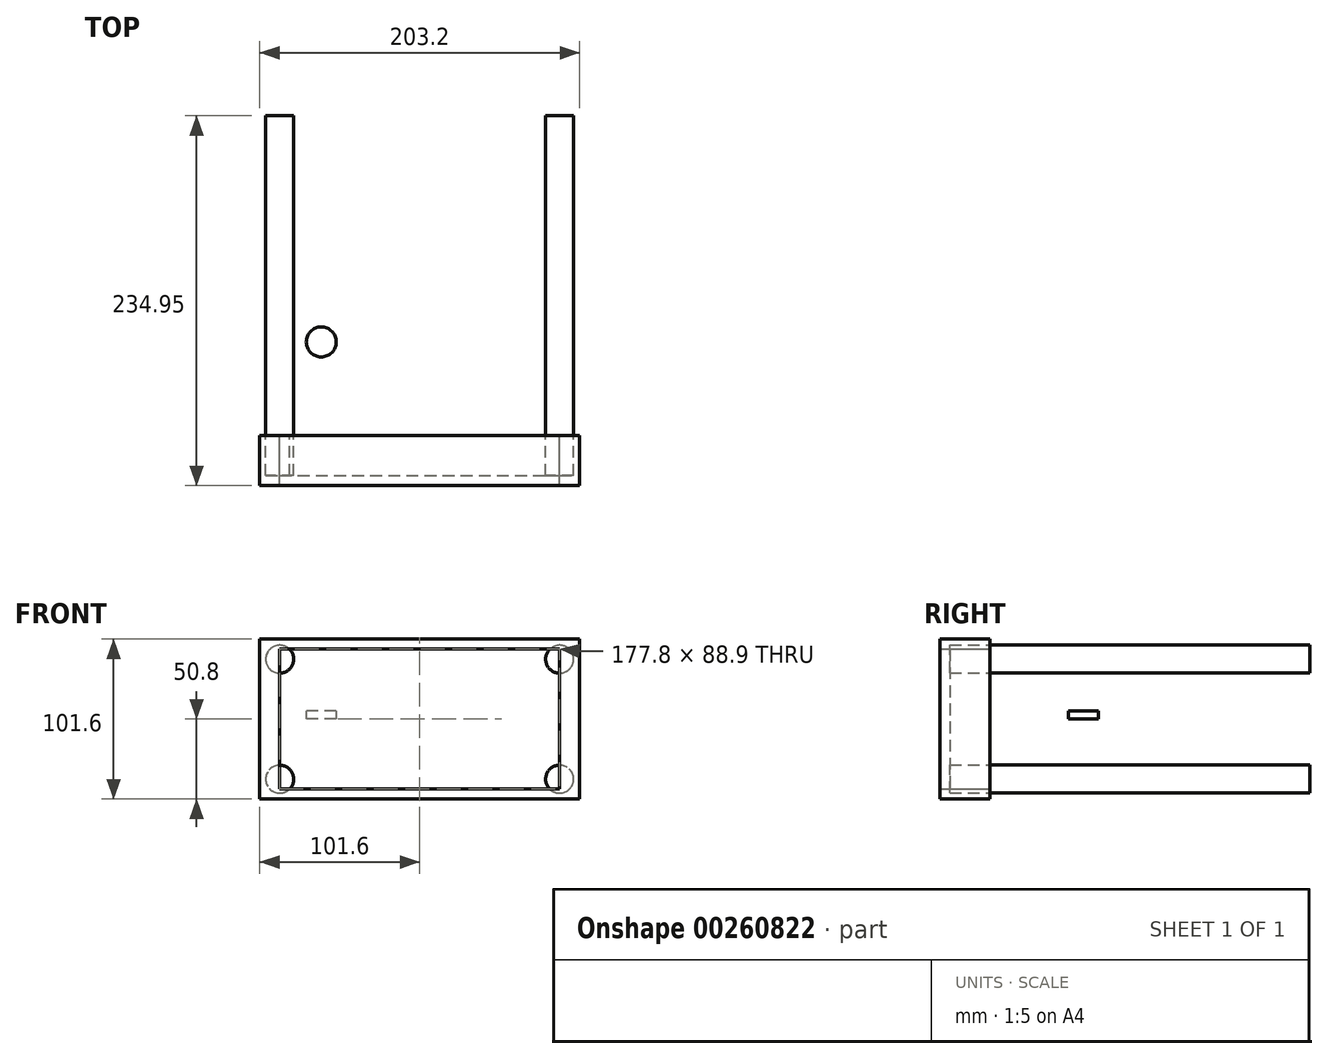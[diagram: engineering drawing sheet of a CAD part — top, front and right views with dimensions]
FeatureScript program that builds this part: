
annotation { "Feature Type Name" : "Feature", "Feature Type Description" : "" }
export const myFeature = defineFeature(function(context is Context, id is Id, definition is map)
    precondition{}
    {
        {
            var Q0;
            Q0=qCreatedBy(makeId("Front.planeOp"),FACE);
            var sketch = newSketch(context, id + "F0", { "sketchPlane" : qUnion([Q0])});
            skLineSegment(sketch, "E0.bottom", {"start": v(-101.6, 50.8) * mm, "end": v(101.6, 50.8) * mm});
            skLineSegment(sketch, "E0.top", {"start": v(-101.6, -50.8) * mm, "end": v(101.6, -50.8) * mm});
            skLineSegment(sketch, "E0.left", {"start": v(-101.6, 50.8) * mm, "end": v(-101.6, -50.8) * mm});
            skLineSegment(sketch, "E0.right", {"start": v(101.6, 50.8) * mm, "end": v(101.6, -50.8) * mm});
            skPoint(sketch, "E0.middle", {"position": v(0, 0) * mm});
            skLineSegment(sketch, "E1.bottom", {"start": v(-88.9, 44.45) * mm, "end": v(88.9, 44.45) * mm});
            skLineSegment(sketch, "E1.top", {"start": v(-88.9, -44.45) * mm, "end": v(88.9, -44.45) * mm});
            skLineSegment(sketch, "E1.left", {"start": v(-88.9, 44.45) * mm, "end": v(-88.9, -44.45) * mm});
            skLineSegment(sketch, "E1.right", {"start": v(88.9, 44.45) * mm, "end": v(88.9, -44.45) * mm});
            skCircle(sketch, "E2", {"center": v(-88.9, 38.1) * mm, "radius": 8.9 * mm});
            skCircle(sketch, "E3", {"center": v(-88.9, -38.1) * mm, "radius": 8.9 * mm});
            skCircle(sketch, "E4", {"center": v(88.9, 38.1) * mm, "radius": 8.9 * mm});
            skCircle(sketch, "E5", {"center": v(88.9, -38.1) * mm, "radius": 8.9 * mm});
            skSolve(sketch);
        }
        {
            var Q0;
            Q0 = qSketchRegion(id + "F0", true);
            var Q1;
            {var subQ0=sQuery(id+"F0.wireOp",EDGE,"E1.left");var subQ1=sQuery(id+"F0.wireOp",EDGE,"E1.bottom");var subQ2=makeQuery(id+"F0.imprint","INTERSECT",VERTEX,{"derivedFrom":[subQ1,subQ0]});Q1=makeQuery(id+"F0.imprint","IMPRINT",FACE,{"disambiguationData":[TD([[makeQuery(id+"F0.imprint","IMPRINT",EDGE,{"disambiguationData":[TD([[subQ2,-1.0]])],"derivedFrom":subQ1}),1.0]])]});}
            var Q2;
            {var subQ0=sQuery(id+"F0.wireOp",EDGE,"E1.left");var subQ1=sQuery(id+"F0.wireOp",EDGE,"E1.top");var subQ2=makeQuery(id+"F0.imprint","INTERSECT",VERTEX,{"derivedFrom":[subQ1,subQ0]});Q2=makeQuery(id+"F0.imprint","IMPRINT",FACE,{"disambiguationData":[TD([[makeQuery(id+"F0.imprint","IMPRINT",EDGE,{"disambiguationData":[TD([[subQ2,-1.0]])],"derivedFrom":subQ1}),-1.0]])]});}
            var Q3;
            {var subQ0=sQuery(id+"F0.wireOp",EDGE,"E1.right");var subQ1=sQuery(id+"F0.wireOp",EDGE,"E1.top");var subQ2=makeQuery(id+"F0.imprint","INTERSECT",VERTEX,{"derivedFrom":[subQ1,subQ0]});Q3=makeQuery(id+"F0.imprint","IMPRINT",FACE,{"disambiguationData":[TD([[makeQuery(id+"F0.imprint","IMPRINT",EDGE,{"disambiguationData":[TD([[subQ2,1.0]])],"derivedFrom":subQ1}),-1.0]])]});}
            var Q4;
            {var subQ0=sQuery(id+"F0.wireOp",EDGE,"E1.right");var subQ1=sQuery(id+"F0.wireOp",EDGE,"E1.bottom");var subQ2=makeQuery(id+"F0.imprint","INTERSECT",VERTEX,{"derivedFrom":[subQ1,subQ0]});Q4=makeQuery(id+"F0.imprint","IMPRINT",FACE,{"disambiguationData":[TD([[makeQuery(id+"F0.imprint","IMPRINT",EDGE,{"disambiguationData":[TD([[subQ2,1.0]])],"derivedFrom":subQ1}),1.0]])]});}
            extrude(context, id + "F1", {"entities" : qUnion([Q0, Q1, Q2, Q3, Q4]), "depth" : 31.75 * mm});
        }
        {
            var Q0;
            Q0=makeQuery(id+"F0.imprint","IMPRINT",FACE,{"disambiguationData":[TD([[makeQuery(id+"F0.imprint","IMPRINT",EDGE,{"derivedFrom":sQuery(id+"F0.wireOp",EDGE,"E1.bottom")}),-1.0]])]});
            var Q1;
            {var subQ0=sQuery(id+"F0.wireOp",EDGE,"E1.right");var subQ1=sQuery(id+"F0.wireOp",EDGE,"E1.bottom");var subQ2=makeQuery(id+"F0.imprint","INTERSECT",VERTEX,{"derivedFrom":[subQ1,subQ0]});Q1=makeQuery(id+"F0.imprint","IMPRINT",FACE,{"disambiguationData":[TD([[makeQuery(id+"F0.imprint","IMPRINT",EDGE,{"disambiguationData":[TD([[subQ2,1.0]])],"derivedFrom":subQ1}),1.0]])]});}
            extrude(context, id + "F2", {"entities" : qUnion([Q0, Q1]), "depth" : 25.4 * mm});
        }
        {
            var Q0;
            {var subQ0=sQuery(id+"F0.wireOp",EDGE,"E1.left");var subQ1=sQuery(id+"F0.wireOp",EDGE,"E1.bottom");var subQ2=makeQuery(id+"F0.imprint","INTERSECT",VERTEX,{"derivedFrom":[subQ1,subQ0]});Q0=makeQuery(id+"F0.imprint","IMPRINT",FACE,{"disambiguationData":[TD([[makeQuery(id+"F0.imprint","IMPRINT",EDGE,{"disambiguationData":[TD([[subQ2,-1.0]])],"derivedFrom":subQ1}),1.0]])]});}
            var Q1;
            {var subQ0=sQuery(id+"F0.wireOp",EDGE,"E1.left");var subQ1=sQuery(id+"F0.wireOp",EDGE,"E1.bottom");var subQ2=makeQuery(id+"F0.imprint","INTERSECT",VERTEX,{"derivedFrom":[subQ1,subQ0]});Q1=makeQuery(id+"F0.imprint","IMPRINT",FACE,{"disambiguationData":[TD([[makeQuery(id+"F0.imprint","IMPRINT",EDGE,{"disambiguationData":[TD([[subQ2,-1.0]])],"derivedFrom":subQ1}),-1.0]])]});}
            var Q2;
            {var subQ0=sQuery(id+"F0.wireOp",EDGE,"E1.left");var subQ1=sQuery(id+"F0.wireOp",EDGE,"E1.top");var subQ2=makeQuery(id+"F0.imprint","INTERSECT",VERTEX,{"derivedFrom":[subQ1,subQ0]});Q2=makeQuery(id+"F0.imprint","IMPRINT",FACE,{"disambiguationData":[TD([[makeQuery(id+"F0.imprint","IMPRINT",EDGE,{"disambiguationData":[TD([[subQ2,-1.0]])],"derivedFrom":subQ1}),-1.0]])]});}
            var Q3;
            {var subQ0=sQuery(id+"F0.wireOp",EDGE,"E1.left");var subQ1=sQuery(id+"F0.wireOp",EDGE,"E1.top");var subQ2=makeQuery(id+"F0.imprint","INTERSECT",VERTEX,{"derivedFrom":[subQ1,subQ0]});Q3=makeQuery(id+"F0.imprint","IMPRINT",FACE,{"disambiguationData":[TD([[makeQuery(id+"F0.imprint","IMPRINT",EDGE,{"disambiguationData":[TD([[subQ2,-1.0]])],"derivedFrom":subQ1}),1.0]])]});}
            var Q4;
            {var subQ0=sQuery(id+"F0.wireOp",EDGE,"E1.right");var subQ1=sQuery(id+"F0.wireOp",EDGE,"E1.top");var subQ2=makeQuery(id+"F0.imprint","INTERSECT",VERTEX,{"derivedFrom":[subQ1,subQ0]});Q4=makeQuery(id+"F0.imprint","IMPRINT",FACE,{"disambiguationData":[TD([[makeQuery(id+"F0.imprint","IMPRINT",EDGE,{"disambiguationData":[TD([[subQ2,1.0]])],"derivedFrom":subQ1}),-1.0]])]});}
            var Q5;
            {var subQ0=sQuery(id+"F0.wireOp",EDGE,"E1.right");var subQ1=sQuery(id+"F0.wireOp",EDGE,"E1.top");var subQ2=makeQuery(id+"F0.imprint","INTERSECT",VERTEX,{"derivedFrom":[subQ1,subQ0]});Q5=makeQuery(id+"F0.imprint","IMPRINT",FACE,{"disambiguationData":[TD([[makeQuery(id+"F0.imprint","IMPRINT",EDGE,{"disambiguationData":[TD([[subQ2,1.0]])],"derivedFrom":subQ1}),1.0]])]});}
            var Q6;
            {var subQ0=sQuery(id+"F0.wireOp",EDGE,"E1.right");var subQ1=sQuery(id+"F0.wireOp",EDGE,"E1.bottom");var subQ2=makeQuery(id+"F0.imprint","INTERSECT",VERTEX,{"derivedFrom":[subQ1,subQ0]});Q6=makeQuery(id+"F0.imprint","IMPRINT",FACE,{"disambiguationData":[TD([[makeQuery(id+"F0.imprint","IMPRINT",EDGE,{"disambiguationData":[TD([[subQ2,1.0]])],"derivedFrom":subQ1}),1.0]])]});}
            var Q7;
            {var subQ0=sQuery(id+"F0.wireOp",EDGE,"E1.right");var subQ1=sQuery(id+"F0.wireOp",EDGE,"E1.bottom");var subQ2=makeQuery(id+"F0.imprint","INTERSECT",VERTEX,{"derivedFrom":[subQ1,subQ0]});Q7=makeQuery(id+"F0.imprint","IMPRINT",FACE,{"disambiguationData":[TD([[makeQuery(id+"F0.imprint","IMPRINT",EDGE,{"disambiguationData":[TD([[subQ2,1.0]])],"derivedFrom":subQ1}),-1.0]])]});}
            extrude(context, id + "F3", {"entities" : qUnion([Q0, Q1, Q2, Q3, Q4, Q5, Q6, Q7]), "oppositeDirection" : true, "depth" : 203.2 * mm});
        }
        {
            var Q0;
            {var subQ5=sQuery(id+"F0.wireOp",EDGE,"E2");var subQ13=sQuery(id+"F0.wireOp",EDGE,"E1.bottom");var subQ14=makeQuery(id+"F0.imprint","INTERSECT",VERTEX,{"derivedFrom":[subQ13,subQ5]});Q0=makeQuery(id+"F0.imprint","IMPRINT",FACE,{"disambiguationData":[TD([[makeQuery(id+"F0.imprint","IMPRINT",EDGE,{"disambiguationData":[TD([[subQ14,-1.0]])],"derivedFrom":subQ13}),-1.0]])]});}
            var Q1;
            {var subQ0=sQuery(id+"F0.wireOp",EDGE,"E1.left");var subQ1=sQuery(id+"F0.wireOp",EDGE,"E1.bottom");var subQ2=makeQuery(id+"F0.imprint","INTERSECT",VERTEX,{"derivedFrom":[subQ1,subQ0]});Q1=makeQuery(id+"F0.imprint","IMPRINT",FACE,{"disambiguationData":[TD([[makeQuery(id+"F0.imprint","IMPRINT",EDGE,{"disambiguationData":[TD([[subQ2,-1.0]])],"derivedFrom":subQ1}),-1.0]])]});}
            var Q2;
            {var subQ0=sQuery(id+"F0.wireOp",EDGE,"E1.left");var subQ1=sQuery(id+"F0.wireOp",EDGE,"E1.top");var subQ2=makeQuery(id+"F0.imprint","INTERSECT",VERTEX,{"derivedFrom":[subQ1,subQ0]});Q2=makeQuery(id+"F0.imprint","IMPRINT",FACE,{"disambiguationData":[TD([[makeQuery(id+"F0.imprint","IMPRINT",EDGE,{"disambiguationData":[TD([[subQ2,-1.0]])],"derivedFrom":subQ1}),1.0]])]});}
            var Q3;
            {var subQ0=sQuery(id+"F0.wireOp",EDGE,"E1.right");var subQ1=sQuery(id+"F0.wireOp",EDGE,"E1.top");var subQ2=makeQuery(id+"F0.imprint","INTERSECT",VERTEX,{"derivedFrom":[subQ1,subQ0]});Q3=makeQuery(id+"F0.imprint","IMPRINT",FACE,{"disambiguationData":[TD([[makeQuery(id+"F0.imprint","IMPRINT",EDGE,{"disambiguationData":[TD([[subQ2,1.0]])],"derivedFrom":subQ1}),1.0]])]});}
            var Q4;
            {var subQ0=sQuery(id+"F0.wireOp",EDGE,"E1.right");var subQ1=sQuery(id+"F0.wireOp",EDGE,"E1.bottom");var subQ2=makeQuery(id+"F0.imprint","INTERSECT",VERTEX,{"derivedFrom":[subQ1,subQ0]});Q4=makeQuery(id+"F0.imprint","IMPRINT",FACE,{"disambiguationData":[TD([[makeQuery(id+"F0.imprint","IMPRINT",EDGE,{"disambiguationData":[TD([[subQ2,1.0]])],"derivedFrom":subQ1}),-1.0]])]});}
            extrude(context, id + "F4", {"entities" : qUnion([Q0, Q1, Q2, Q3, Q4]), "depth" : 25.4 * mm});
        }
        {
            var Q0;
            Q0=makeQuery(id+"F3.opExtrude","CAP_FACE",FACE,{"disambiguationData":[OSD([sQuery(id+"F0.wireOp",EDGE,"E5")])],"isStart":true});
            extrude(context, id + "F5", {"entities" : qUnion([Q0]), "depth" : 25.4 * mm});
        }
        {
            var Q0;
            Q0=makeQuery(id+"F3.opExtrude","CAP_FACE",FACE,{"disambiguationData":[OSD([sQuery(id+"F0.wireOp",EDGE,"E3")])],"isStart":true});
            var Q1;
            Q1=makeQuery(id+"F3.opExtrude","CAP_FACE",FACE,{"disambiguationData":[OSD([sQuery(id+"F0.wireOp",EDGE,"E2")])],"isStart":true});
            extrude(context, id + "F6", {"entities" : qUnion([Q0, Q1]), "depth" : 25.4 * mm});
        }
        {
            var Q0;
            Q0=qCreatedBy(makeId("Top.planeOp"),FACE);
            var sketch = newSketch(context, id + "F7", { "sketchPlane" : qUnion([Q0])});
            skCircle(sketch, "E6", {"center": v(-62.5, 59.55) * mm, "radius": 9.53 * mm});
            skSolve(sketch);
        }
        {
            var Q0;
            Q0 = qSketchRegion(id + "F7", true);
            extrude(context, id + "F8", {"entities" : qUnion([Q0]), "depth" : 5.08 * mm});
        }
    });
